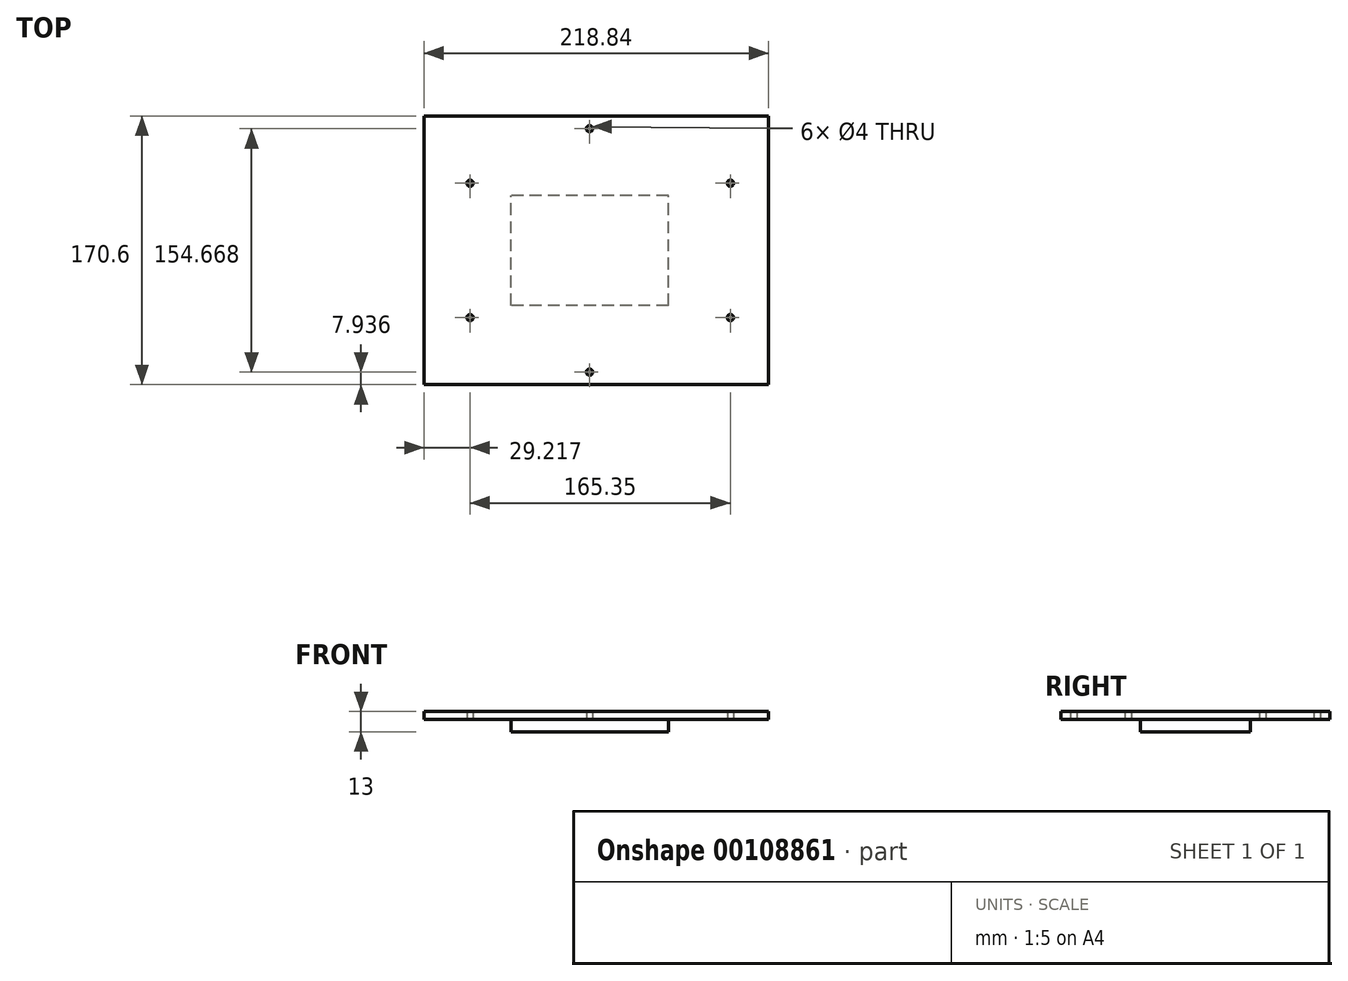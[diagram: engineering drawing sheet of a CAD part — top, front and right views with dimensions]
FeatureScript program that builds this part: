
annotation { "Feature Type Name" : "Feature", "Feature Type Description" : "" }
export const myFeature = defineFeature(function(context is Context, id is Id, definition is map)
    precondition{}
    {
        {
            var Q0;
            Q0=qCreatedBy(makeId("Top.planeOp"),FACE);
            var sketch = newSketch(context, id + "F0", { "sketchPlane" : qUnion([Q0])});
            skLineSegment(sketch, "E0.bottom", {"start": v(-105.1, 85.33) * mm, "end": v(113.74, 85.33) * mm});
            skLineSegment(sketch, "E0.top", {"start": v(-105.1, -85.27) * mm, "end": v(113.74, -85.27) * mm});
            skLineSegment(sketch, "E0.left", {"start": v(-105.1, 85.33) * mm, "end": v(-105.1, -85.27) * mm});
            skLineSegment(sketch, "E0.right", {"start": v(113.74, 85.33) * mm, "end": v(113.74, -85.27) * mm});
            skLineSegment(sketch, "E1", {"start": v(-116.56, 77.33) * mm, "end": v(142.19, 77.33) * mm, "construction": true});
            skLineSegment(sketch, "E2", {"start": v(-122.4, -77.33) * mm, "end": v(166.84, -77.33) * mm, "construction": true});
            skLineSegment(sketch, "E3", {"start": v(-105.1, -12.17) * mm, "end": v(-105.1, 146.5) * mm, "construction": true});
            skLineSegment(sketch, "E4", {"start": v(113.74, -8.47) * mm, "end": v(113.74, 146.87) * mm, "construction": true});
            skLineSegment(sketch, "E5", {"start": v(-75.88, 139.76) * mm, "end": v(-75.88, -106.4) * mm, "construction": true});
            skLineSegment(sketch, "E6", {"start": v(89.47, 134.57) * mm, "end": v(89.47, -101.58) * mm, "construction": true});
            skLineSegment(sketch, "E7", {"start": v(0, 0) * mm, "end": v(0, 119.26) * mm, "construction": true});
            skLineSegment(sketch, "E8", {"start": v(-127.17, 0) * mm, "end": v(140.24, 0) * mm, "construction": true});
            skPoint(sketch, "E9", {"position": v(0, 77.33) * mm});
            skLineSegment(sketch, "E10", {"start": v(0, 0) * mm, "end": v(0, -77.33) * mm, "construction": true});
            skPoint(sketch, "E11", {"position": v(0, -77.33) * mm});
            skLineSegment(sketch, "E12", {"start": v(-153.1, 42.67) * mm, "end": v(139.92, 42.67) * mm, "construction": true});
            skLineSegment(sketch, "E13", {"start": v(-125.43, -42.67) * mm, "end": v(144.25, -42.67) * mm, "construction": true});
            skPoint(sketch, "E14", {"position": v(-75.88, 42.67) * mm});
            skPoint(sketch, "E15", {"position": v(89.47, 42.67) * mm});
            skPoint(sketch, "E16", {"position": v(-75.88, -42.67) * mm});
            skPoint(sketch, "E17", {"position": v(89.47, -42.67) * mm});
            skLineSegment(sketch, "E18", {"start": v(-120.4, -60) * mm, "end": v(122.27, -60) * mm, "construction": true});
            skLineSegment(sketch, "E19", {"start": v(-111.93, 60) * mm, "end": v(122.54, 60) * mm, "construction": true});
            skSolve(sketch);
        }
        {
            var Q0;
            Q0=makeQuery(id+"F0.imprint","IMPRINT",FACE,{"disambiguationData":[TD([[makeQuery(id+"F0.imprint","IMPRINT",EDGE,{"derivedFrom":sQuery(id+"F0.wireOp",EDGE,"E0.bottom")}),-1.0]])]});
            extrude(context, id + "F1", {"entities" : qUnion([Q0]), "depth" : 5 * mm});
        }
        {
            var Q0;
            Q0=sQuery(id+"F0.wireOp",VERTEX,"E14");
            var Q1;
            Q1=sQuery(id+"F0.wireOp",VERTEX,"E9");
            var Q2;
            Q2=sQuery(id+"F0.wireOp",VERTEX,"E15");
            var Q3;
            Q3=sQuery(id+"F0.wireOp",VERTEX,"E16");
            var Q4;
            Q4=sQuery(id+"F0.wireOp",VERTEX,"E11");
            var Q5;
            Q5=sQuery(id+"F0.wireOp",VERTEX,"E17");
            var Q6;
            Q6=makeQuery(id+"F1.opExtrude","SWEPT_BODY",BODY,{"disambiguationData":[OSD([sQuery(id+"F0.wireOp",EDGE,"E0.bottom"),sQuery(id+"F0.wireOp",EDGE,"E0.top"),sQuery(id+"F0.wireOp",EDGE,"E0.left"),sQuery(id+"F0.wireOp",EDGE,"E0.right")])]});
            hole(context, id + "F2", {"style" : HoleStyle.SIMPLE, "endStyle" : HoleEndStyle.THROUGH, "oppositeDirection" : true, "holeDiameter" : 4 * mm, "startFromSketch" : true, "locations" : qUnion([Q0, Q1, Q2, Q3, Q4, Q5]), "scope" : qUnion([Q6]), "isTappedThrough" : true});
        }
        {
            var Q0;
            Q0=qCreatedBy(makeId("Right.planeOp"),FACE);
            var sketch = newSketch(context, id + "F3", { "sketchPlane" : qUnion([Q0])});
            skLineSegment(sketch, "E20", {"start": v(0, -7.84) * mm, "end": v(0, 9.42) * mm, "construction": true});
            skLineSegment(sketch, "E21", {"start": v(-5.84, 9.06) * mm, "end": v(-5.84, -8.05) * mm, "construction": true});
            skLineSegment(sketch, "E22", {"start": v(5.84, 9.42) * mm, "end": v(5.84, -7.66) * mm, "construction": true});
            skLineSegment(sketch, "E23.bottom", {"start": v(-35, 0) * mm, "end": v(35, 0) * mm});
            skLineSegment(sketch, "E23.top", {"start": v(-35, -8) * mm, "end": v(35, -8) * mm});
            skLineSegment(sketch, "E23.left", {"start": v(-35, 0) * mm, "end": v(-35, -8) * mm});
            skLineSegment(sketch, "E23.right", {"start": v(35, 0) * mm, "end": v(35, -8) * mm});
            skSolve(sketch);
        }
        {
            var Q0;
            Q0=makeQuery(id+"F3.imprint","IMPRINT",FACE,{"disambiguationData":[TD([[makeQuery(id+"F3.imprint","IMPRINT",EDGE,{"derivedFrom":sQuery(id+"F3.wireOp",EDGE,"E23.bottom")}),-1.0]])]});
            extrude(context, id + "F4", {"entities" : qUnion([Q0]), "operationType" : NewBodyOperationType.ADD, "endBound" : BoundingType.SYMMETRIC, "depth" : 100 * mm});
        }
    });
